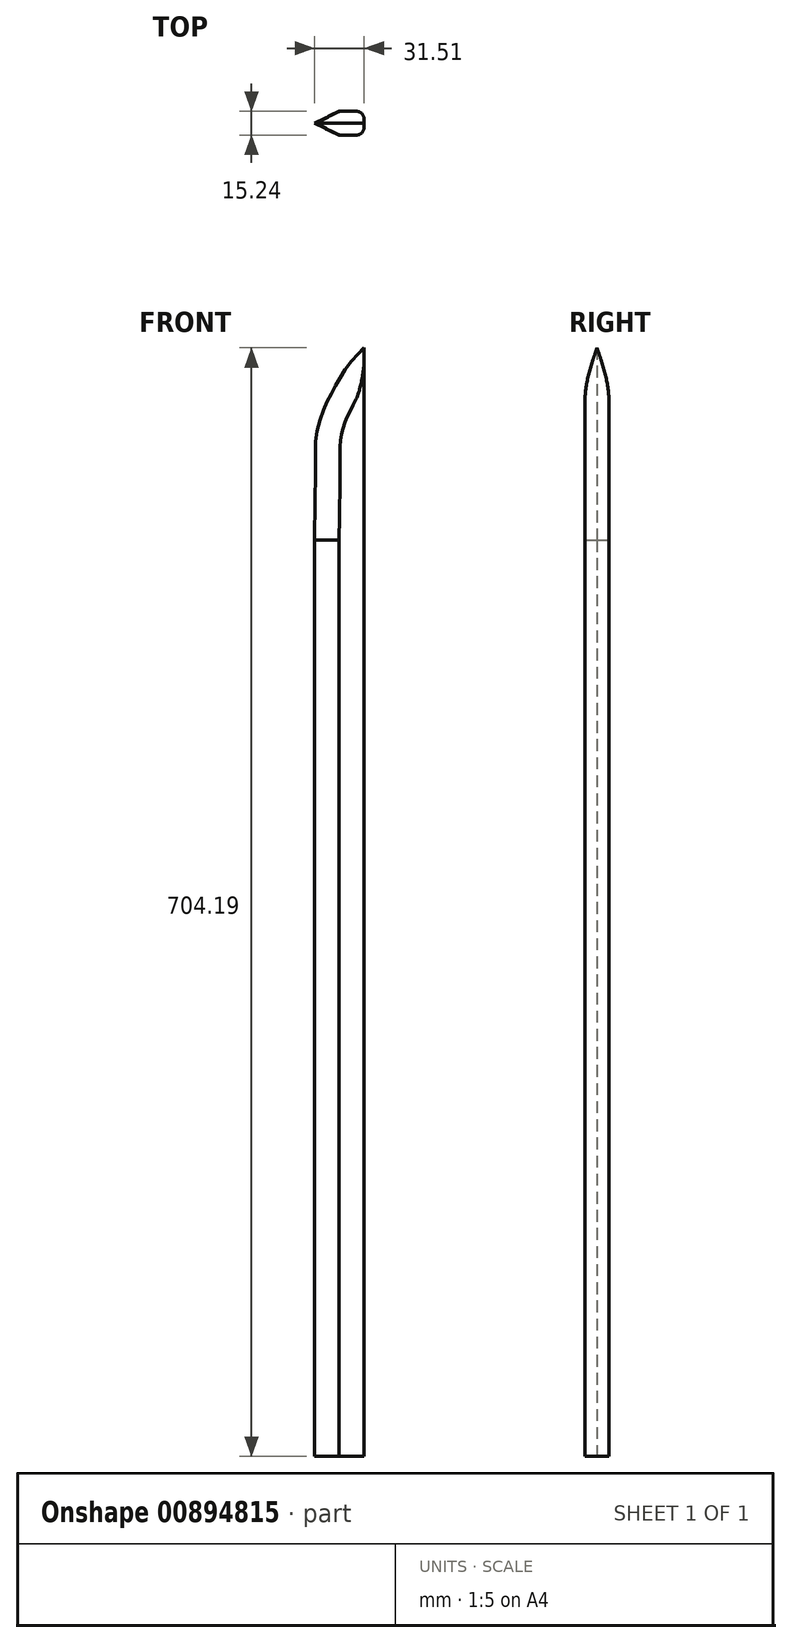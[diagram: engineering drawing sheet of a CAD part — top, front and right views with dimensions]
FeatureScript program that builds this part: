
annotation { "Feature Type Name" : "Feature", "Feature Type Description" : "" }
export const myFeature = defineFeature(function(context is Context, id is Id, definition is map)
    precondition{}
    {
        {
            var Q0;
            Q0=qCreatedBy(makeId("Front.planeOp"),FACE);
            var sketch = newSketch(context, id + "F0", { "sketchPlane" : qUnion([Q0])});
            skLineSegment(sketch, "E0", {"start": v(-12.43, 147.36) * mm, "end": v(-12.43, 694.5) * mm});
            skLineSegment(sketch, "E1", {"start": v(19.08, 182.02) * mm, "end": v(19.08, 816.67) * mm});
            skLineSegment(sketch, "E2", {"start": v(-12.43, 147.36) * mm, "end": v(-12.43, 112.48) * mm});
            skLineSegment(sketch, "E3", {"start": v(19.08, 182.02) * mm, "end": v(19.08, 112.48) * mm});
            skLineSegment(sketch, "E4", {"start": v(19.08, 112.48) * mm, "end": v(-12.43, 112.48) * mm});
            skFitSpline(sketch, "E5", {"points": [v(19.08, 816.67) * mm, v(9, 805.47) * mm, v(0, 790.9) * mm, v(-10.04, 767.38) * mm, v(-11.9, 747.6) * mm, v(-11.9, 730.42) * mm, v(-12.43, 694.5) * mm], "startDerivative": vector(-75.25, -77.3) * mm, "endDerivative": vector(-3.24, -182.15) * mm});
            skSolve(sketch);
        }
        {
            var Q0;
            Q0=makeQuery(id+"F0.imprint","IMPRINT",FACE,{"disambiguationData":[TD([[makeQuery(id+"F0.imprint","IMPRINT",EDGE,{"derivedFrom":sQuery(id+"F0.wireOp",EDGE,"E0")}),-1.0]])]});
            extrude(context, id + "F1", {"entities" : qUnion([Q0]), "depth" : 7.62 * mm, "offsetDistance" : 25.4 * mm});
        }
        {
            var Q0;
            Q0=makeQuery(id+"F1.opExtrude","CAP_FACE",FACE,{"disambiguationData":[OSD([sQuery(id+"F0.wireOp",EDGE,"E0"),sQuery(id+"F0.wireOp",EDGE,"E1"),sQuery(id+"F0.wireOp",EDGE,"55b54924-0589-4df6-90b1-72972e55ac43"),sQuery(id+"F0.wireOp",EDGE,"E2"),sQuery(id+"F0.wireOp",EDGE,"E3"),sQuery(id+"F0.wireOp",EDGE,"E4")])],"isStart":true});
            extrude(context, id + "F2", {"entities" : qUnion([Q0]), "operationType" : NewBodyOperationType.ADD, "depth" : 7.62 * mm, "offsetDistance" : 25.4 * mm});
        }
        {
            var Q0;
            Q0=makeQuery(id+"F2.opExtrude","CAP_EDGE",EDGE,{"disambiguationData":[OSD([sQuery(id+"F0.wireOp",EDGE,"E5")])],"isStart":false});
            var Q1;
            Q1=makeQuery(id+"F1.opExtrude","CAP_EDGE",EDGE,{"disambiguationData":[OSD([sQuery(id+"F0.wireOp",EDGE,"E5")])],"isStart":false});
            var Q2;
            Q2=makeQuery(id+"F1.opExtrude","CAP_EDGE",EDGE,{"disambiguationData":[OSD([sQuery(id+"F0.wireOp",EDGE,"E0"),sQuery(id+"F0.wireOp",EDGE,"E2")])],"isStart":false});
            var Q3;
            Q3=makeQuery(id+"F2.opExtrude","CAP_EDGE",EDGE,{"disambiguationData":[OSD([sQuery(id+"F0.wireOp",EDGE,"E0"),sQuery(id+"F0.wireOp",EDGE,"E2")])],"isStart":false});
            chamfer(context, id + "F3", {"entities" : qUnion([Q0, Q1, Q2, Q3]), "chamferType" : ChamferType.OFFSET_ANGLE, "width" : 7.62 * mm, "oppositeDirection" : false, "angle" : 64 * degree, "tangentPropagation" : true});
        }
        {
            var Q0;
            Q0=makeQuery(id+"F1.opExtrude","CAP_EDGE",EDGE,{"disambiguationData":[OSD([sQuery(id+"F0.wireOp",EDGE,"E1"),sQuery(id+"F0.wireOp",EDGE,"E3")])],"isStart":false});
            var Q1;
            Q1=makeQuery(id+"F2.opExtrude","CAP_EDGE",EDGE,{"disambiguationData":[OSD([sQuery(id+"F0.wireOp",EDGE,"E1"),sQuery(id+"F0.wireOp",EDGE,"E3")])],"isStart":false});
            fillet(context, id + "F4", {"entities" : qUnion([Q0, Q1]), "radius" : 5.08 * mm, "tangentPropagation" : true, "allowEdgeOverflow" : false});
        }
    });
